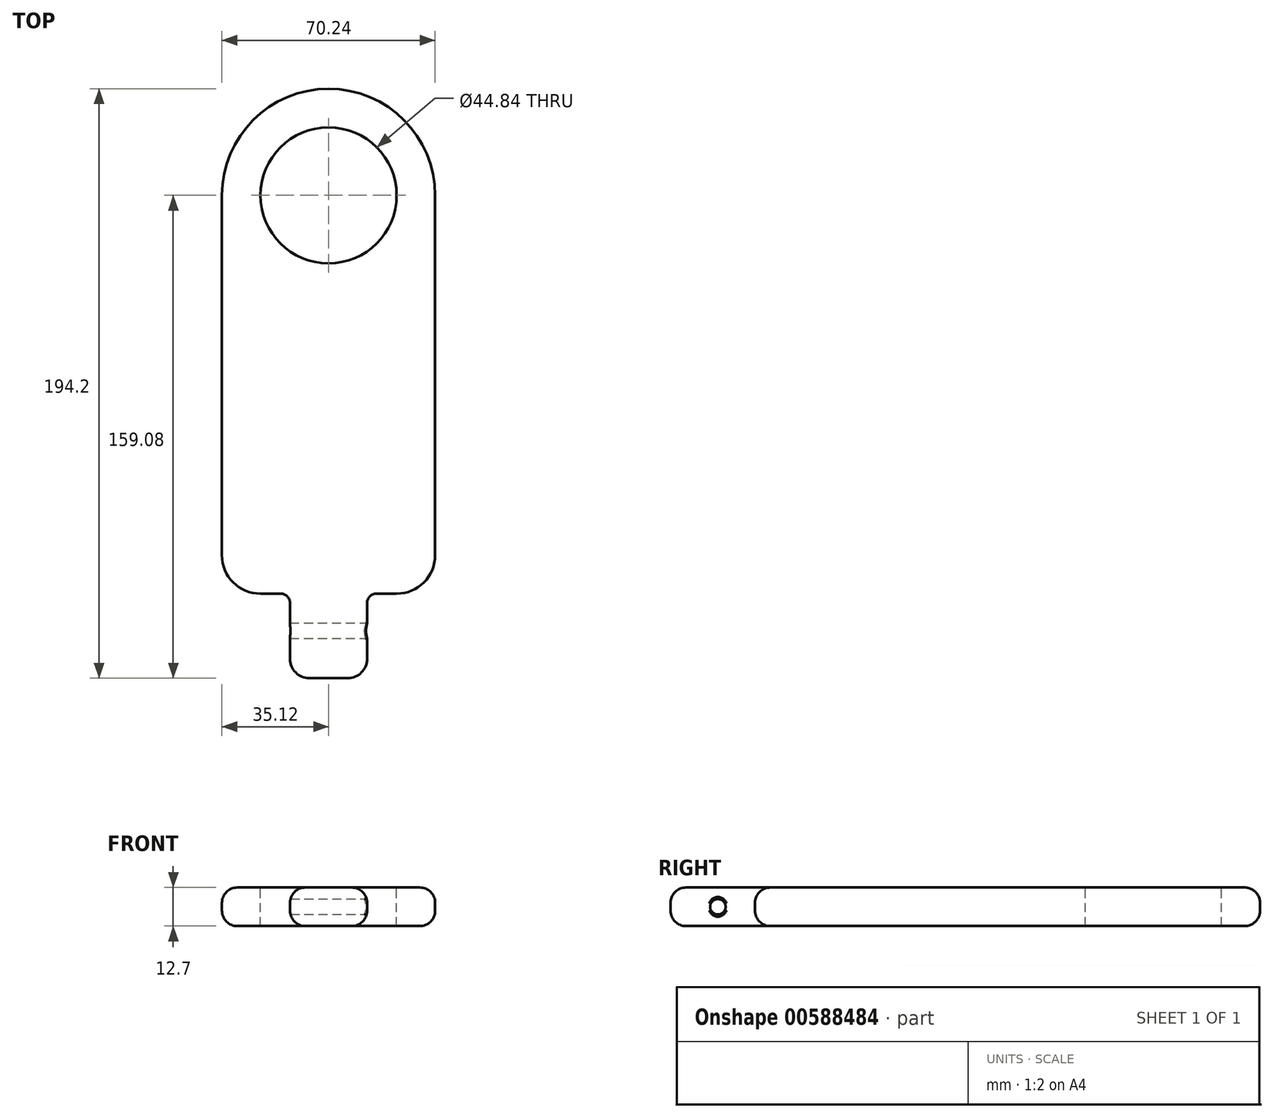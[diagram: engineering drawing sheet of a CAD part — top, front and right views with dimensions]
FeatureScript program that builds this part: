
annotation { "Feature Type Name" : "Feature", "Feature Type Description" : "" }
export const myFeature = defineFeature(function(context is Context, id is Id, definition is map)
    precondition{}
    {
        {
            var Q0;
            Q0=qCreatedBy(makeId("Top.planeOp"),FACE);
            var sketch = newSketch(context, id + "F0", { "sketchPlane" : qUnion([Q0])});
            skLineSegment(sketch, "E0.bottom", {"start": v(-35.12, 65.63) * mm, "end": v(35.12, 65.63) * mm});
            skLineSegment(sketch, "E0.top", {"start": v(-22.42, -65.63) * mm, "end": v(-15.73, -65.63) * mm});
            skLineSegment(sketch, "E0.left", {"start": v(-35.12, 65.63) * mm, "end": v(-35.12, -52.93) * mm});
            skLineSegment(sketch, "E0.right", {"start": v(35.12, 65.63) * mm, "end": v(35.12, -52.93) * mm});
            skPoint(sketch, "E0.middle", {"position": v(0, 0) * mm});
            skCircle(sketch, "E1", {"center": v(0, 65.63) * mm, "radius": 35.12 * mm});
            skLineSegment(sketch, "E2.bottom", {"start": v(-6.35, -93.45) * mm, "end": v(6.35, -93.45) * mm});
            skLineSegment(sketch, "E2.left", {"start": v(-12.7, -87.1) * mm, "end": v(-12.7, -68.66) * mm});
            skLineSegment(sketch, "E2.right", {"start": v(12.7, -87.1) * mm, "end": v(12.7, -68.66) * mm});
            skPoint(sketch, "E2.middle", {"position": v(0, -65.63) * mm});
            skPoint(sketch, "E3.visualSharp", {"position": v(-12.7, -93.45) * mm});
            skArc(sketch, "E3.filletArc", {"start": v(-12.7, -87.1) * mm, "mid": v(-10.84, -91.6) * mm, "end": v(-6.35, -93.45) * mm});
            skPoint(sketch, "E4.visualSharp", {"position": v(12.7, -93.45) * mm});
            skArc(sketch, "E4.filletArc", {"start": v(6.35, -93.45) * mm, "mid": v(10.84, -91.6) * mm, "end": v(12.7, -87.1) * mm});
            skPoint(sketch, "E5.visualSharp", {"position": v(-35.12, -65.63) * mm});
            skArc(sketch, "E5.filletArc", {"start": v(-35.12, -52.93) * mm, "mid": v(-31.4, -61.91) * mm, "end": v(-22.42, -65.63) * mm});
            skPoint(sketch, "E6.visualSharp", {"position": v(35.12, -65.63) * mm});
            skArc(sketch, "E6.filletArc", {"start": v(22.42, -65.63) * mm, "mid": v(31.4, -61.91) * mm, "end": v(35.12, -52.93) * mm});
            skArc(sketch, "E7.filletArc", {"start": v(-12.7, -68.66) * mm, "mid": v(-13.59, -66.52) * mm, "end": v(-15.73, -65.63) * mm});
            skLineSegment(sketch, "E8", {"start": v(15.73, -65.63) * mm, "end": v(22.42, -65.63) * mm});
            skPoint(sketch, "E9.visualSharp", {"position": v(12.7, -65.63) * mm});
            skArc(sketch, "E9.filletArc", {"start": v(15.73, -65.63) * mm, "mid": v(13.59, -66.52) * mm, "end": v(12.7, -68.66) * mm});
            skSolve(sketch);
        }
        {
            var Q0;
            {var subQ0=sQuery(id+"F0.wireOp",EDGE,"E0.bottom");Q0=makeQuery(id+"F0.imprint","IMPRINT",FACE,{"disambiguationData":[TD([[makeQuery(id+"F0.imprint","IMPRINT",EDGE,{"derivedFrom":subQ0}),1.0]])]});}
            var Q1;
            {var subQ0=sQuery(id+"F0.wireOp",EDGE,"E0.bottom");Q1=makeQuery(id+"F0.imprint","IMPRINT",FACE,{"disambiguationData":[TD([[makeQuery(id+"F0.imprint","IMPRINT",EDGE,{"derivedFrom":subQ0}),-1.0]])]});}
            var Q2;
            Q2=makeQuery(id+"F0.imprint","IMPRINT",FACE,{"disambiguationData":[TD([[makeQuery(id+"F0.imprint","IMPRINT",EDGE,{"derivedFrom":sQuery(id+"F0.wireOp",EDGE,"E0.top")}),1.0]])]});
            var Q3;
            Q3=makeQuery(id+"F0.imprint","IMPRINT",FACE,{"disambiguationData":[TD([[makeQuery(id+"F0.imprint","IMPRINT",EDGE,{"derivedFrom":sQuery(id+"F0.wireOp",EDGE,"E2.bottom")}),1.0]])]});
            extrude(context, id + "F1", {"entities" : qUnion([Q0, Q1, Q2, Q3]), "depth" : 12.7 * mm, "offsetDistance" : 25.4 * mm});
        }
        {
            var Q0;
            Q0=makeQuery(id+"F1.opExtrude","CAP_FACE",FACE,{"disambiguationData":[OSD([sQuery(id+"F0.wireOp",EDGE,"E0.top"),sQuery(id+"F0.wireOp",EDGE,"E0.left"),sQuery(id+"F0.wireOp",EDGE,"E0.right"),sQuery(id+"F0.wireOp",EDGE,"E1")])],"isStart":false});
            var sketch = newSketch(context, id + "F2", { "sketchPlane" : qUnion([Q0])});
            skCircle(sketch, "E10", {"center": v(0, 65.63) * mm, "radius": 22.42 * mm});
            skSolve(sketch);
        }
        {
            var Q0;
            Q0 = qSketchRegion(id + "F2", true);
            extrude(context, id + "F3", {"entities" : qUnion([Q0]), "operationType" : NewBodyOperationType.REMOVE, "endBound" : BoundingType.UP_TO_NEXT, "oppositeDirection" : true, "depth" : 25.4 * mm, "offsetDistance" : 25.4 * mm});
        }
        {
            var Q0;
            Q0=makeQuery(id+"F1.opExtrude","CAP_EDGE",EDGE,{"disambiguationData":[OSD([sQuery(id+"F0.wireOp",EDGE,"E0.right")])],"isStart":false});
            var Q1;
            Q1=makeQuery(id+"F1.opExtrude","CAP_EDGE",EDGE,{"disambiguationData":[OSD([sQuery(id+"F0.wireOp",EDGE,"E1")])],"isStart":true});
            var Q2;
            Q2=makeQuery(id+"F3.boolean.opBoolean","COPY",EDGE,{"derivedFrom":makeQuery(id+"F3.opExtrude","CAP_EDGE",EDGE,{"disambiguationData":[OSD([sQuery(id+"F2.wireOp",EDGE,"E10")])],"isStart":true})});
            fillet(context, id + "F4", {"entities" : qUnion([Q0, Q1, Q2]), "radius" : 5.08 * mm, "tangentPropagation" : true, "allowEdgeOverflow" : false});
        }
        {
            var Q0;
            Q0=makeQuery(id+"F1.opExtrude","SWEPT_FACE",FACE,{"disambiguationData":[OSD([sQuery(id+"F0.wireOp",EDGE,"E2.right")])]});
            var sketch = newSketch(context, id + "F5", { "sketchPlane" : qUnion([Q0])});
            skCircle(sketch, "E11", {"center": v(-77.88, 6.35) * mm, "radius": 2.54 * mm});
            skPoint(sketch, "E11.centerSnap0", {"position": v(-87.1, 6.35) * mm});
            skPoint(sketch, "E11.centerSnap1", {"position": v(-77.88, 5.08) * mm});
            skSolve(sketch);
        }
        {
            var Q0;
            Q0 = qSketchRegion(id + "F5", true);
            extrude(context, id + "F6", {"entities" : qUnion([Q0]), "operationType" : NewBodyOperationType.REMOVE, "endBound" : BoundingType.UP_TO_NEXT, "oppositeDirection" : true, "depth" : 25.4 * mm, "offsetDistance" : 25.4 * mm});
        }
        {
            var Q0;
            Q0=makeQuery(id+"F6.boolean.opBoolean","COPY",EDGE,{"disambiguationData":[OD(1.0)],"derivedFrom":makeQuery(id+"F6.opExtrude","CAP_EDGE",EDGE,{"disambiguationData":[OSD([sQuery(id+"F5.wireOp",EDGE,"E11")])],"isStart":true})});
            var Q1;
            {var subQ0=sQuery(id+"F0.wireOp",EDGE,"E2.right");Q1=makeQuery(id+"F6.boolean.opBoolean","INTERSECT",EDGE,{"derivedFrom":[makeQuery(id+"F4.opFillet","BLEND_FACE",FACE,{"disambiguationData":[OSD([subQ0]),TDD([makeQuery(id+"F1.opExtrude","CAP_EDGE",EDGE,{"disambiguationData":[OSD([subQ0])],"isStart":false})])]}),makeQuery(id+"F6.opExtrude","SWEPT_FACE",FACE,{"disambiguationData":[OSD([sQuery(id+"F5.wireOp",EDGE,"E11")])]})]});}
            var Q2;
            Q2=makeQuery(id+"F6.boolean.opBoolean","COPY",EDGE,{"disambiguationData":[OD(0.0)],"derivedFrom":makeQuery(id+"F6.opExtrude","CAP_EDGE",EDGE,{"disambiguationData":[OSD([sQuery(id+"F5.wireOp",EDGE,"E11")])],"isStart":true})});
            var Q3;
            {var subQ0=sQuery(id+"F0.wireOp",EDGE,"E2.right");Q3=makeQuery(id+"F6.boolean.opBoolean","INTERSECT",EDGE,{"derivedFrom":[makeQuery(id+"F4.opFillet","BLEND_FACE",FACE,{"disambiguationData":[OSD([subQ0]),TDD([makeQuery(id+"F1.opExtrude","CAP_EDGE",EDGE,{"disambiguationData":[OSD([subQ0])],"isStart":true})])]}),makeQuery(id+"F6.opExtrude","SWEPT_FACE",FACE,{"disambiguationData":[OSD([sQuery(id+"F5.wireOp",EDGE,"E11")])]})]});}
            var Q4;
            {var subQ0=sQuery(id+"F5.wireOp",EDGE,"E11");var subQ1=sQuery(id+"F0.wireOp",EDGE,"E2.right");var subQ2=makeQuery(id+"F1.opExtrude","SWEPT_FACE",FACE,{"disambiguationData":[OSD([subQ1])]});var subQ3=makeQuery(id+"F4.opFillet","BLEND_EDGE",EDGE,{"blendedFrom":[makeQuery(id+"F1.opExtrude","CAP_EDGE",EDGE,{"disambiguationData":[OSD([subQ1])],"isStart":false}),subQ2],"blendedInto":[subQ2]});var subQ4=makeQuery(id+"F5.imprint","INTERSECT",VERTEX,{"disambiguationData":[OD(1.0)],"derivedFrom":[subQ3,subQ0]});var subQ5=makeQuery(id+"F4.opFillet","BLEND_EDGE",EDGE,{"blendedFrom":[makeQuery(id+"F1.opExtrude","CAP_EDGE",EDGE,{"disambiguationData":[OSD([subQ1])],"isStart":true}),subQ2],"blendedInto":[subQ2]});var subQ7=makeQuery(id+"F5.imprint","INTERSECT",VERTEX,{"disambiguationData":[OD(0.0)],"derivedFrom":[subQ5,subQ0]});var subQ8=makeQuery(id+"F5.imprint","INTERSECT",VERTEX,{"disambiguationData":[OD(0.0)],"derivedFrom":[subQ3,subQ0]});var subQ9=sQuery(id+"F0.wireOp",EDGE,"E2.left");Q4=makeQuery(id+"F6.boolean.opBoolean","COPY",EDGE,{"derivedFrom":makeQuery(id+"F6.opExtrude","TWEAK_EDGE",EDGE,{"derivedFrom":[makeQuery(id+"F4.opFillet","BLEND_FACE",FACE,{"disambiguationData":[OSD([subQ9]),TDD([makeQuery(id+"F1.opExtrude","CAP_EDGE",EDGE,{"disambiguationData":[OSD([subQ9])],"isStart":false})])]}),makeQuery(id+"F5.imprint","IMPRINT",EDGE,{"disambiguationData":[TD([[subQ8,1.0]])],"derivedFrom":subQ0}),makeQuery(id+"F5.imprint","IMPRINT",EDGE,{"disambiguationData":[TD([[subQ8,-1.0]])],"derivedFrom":subQ0}),makeQuery(id+"F5.imprint","IMPRINT",EDGE,{"disambiguationData":[TD([[subQ7,-1.0]])],"derivedFrom":subQ0}),makeQuery(id+"F5.imprint","IMPRINT",EDGE,{"disambiguationData":[TD([[subQ4,1.0]])],"derivedFrom":subQ0})]})});}
            var Q5;
            {var subQ0=sQuery(id+"F5.wireOp",EDGE,"E11");var subQ1=sQuery(id+"F0.wireOp",EDGE,"E2.right");var subQ2=makeQuery(id+"F1.opExtrude","SWEPT_FACE",FACE,{"disambiguationData":[OSD([subQ1])]});var subQ3=makeQuery(id+"F4.opFillet","BLEND_EDGE",EDGE,{"blendedFrom":[makeQuery(id+"F1.opExtrude","CAP_EDGE",EDGE,{"disambiguationData":[OSD([subQ1])],"isStart":false}),subQ2],"blendedInto":[subQ2]});var subQ4=makeQuery(id+"F5.imprint","INTERSECT",VERTEX,{"disambiguationData":[OD(1.0)],"derivedFrom":[subQ3,subQ0]});var subQ5=makeQuery(id+"F4.opFillet","BLEND_EDGE",EDGE,{"blendedFrom":[makeQuery(id+"F1.opExtrude","CAP_EDGE",EDGE,{"disambiguationData":[OSD([subQ1])],"isStart":true}),subQ2],"blendedInto":[subQ2]});var subQ7=makeQuery(id+"F5.imprint","INTERSECT",VERTEX,{"disambiguationData":[OD(0.0)],"derivedFrom":[subQ5,subQ0]});var subQ8=makeQuery(id+"F5.imprint","INTERSECT",VERTEX,{"disambiguationData":[OD(0.0)],"derivedFrom":[subQ3,subQ0]});Q5=makeQuery(id+"F6.boolean.opBoolean","COPY",EDGE,{"derivedFrom":makeQuery(id+"F6.opExtrude","TWEAK_EDGE",EDGE,{"disambiguationData":[OD(1.0)],"derivedFrom":[makeQuery(id+"F1.opExtrude","SWEPT_FACE",FACE,{"disambiguationData":[OSD([sQuery(id+"F0.wireOp",EDGE,"E2.left")])]}),makeQuery(id+"F5.imprint","IMPRINT",EDGE,{"disambiguationData":[TD([[subQ8,1.0]])],"derivedFrom":subQ0}),makeQuery(id+"F5.imprint","IMPRINT",EDGE,{"disambiguationData":[TD([[subQ8,-1.0]])],"derivedFrom":subQ0}),makeQuery(id+"F5.imprint","IMPRINT",EDGE,{"disambiguationData":[TD([[subQ7,-1.0]])],"derivedFrom":subQ0}),makeQuery(id+"F5.imprint","IMPRINT",EDGE,{"disambiguationData":[TD([[subQ4,1.0]])],"derivedFrom":subQ0})]})});}
            fillet(context, id + "F7", {"entities" : qUnion([Q0, Q1, Q2, Q3, Q4, Q5]), "radius" : 0.5 * mm, "tangentPropagation" : true, "allowEdgeOverflow" : false});
        }
    });
